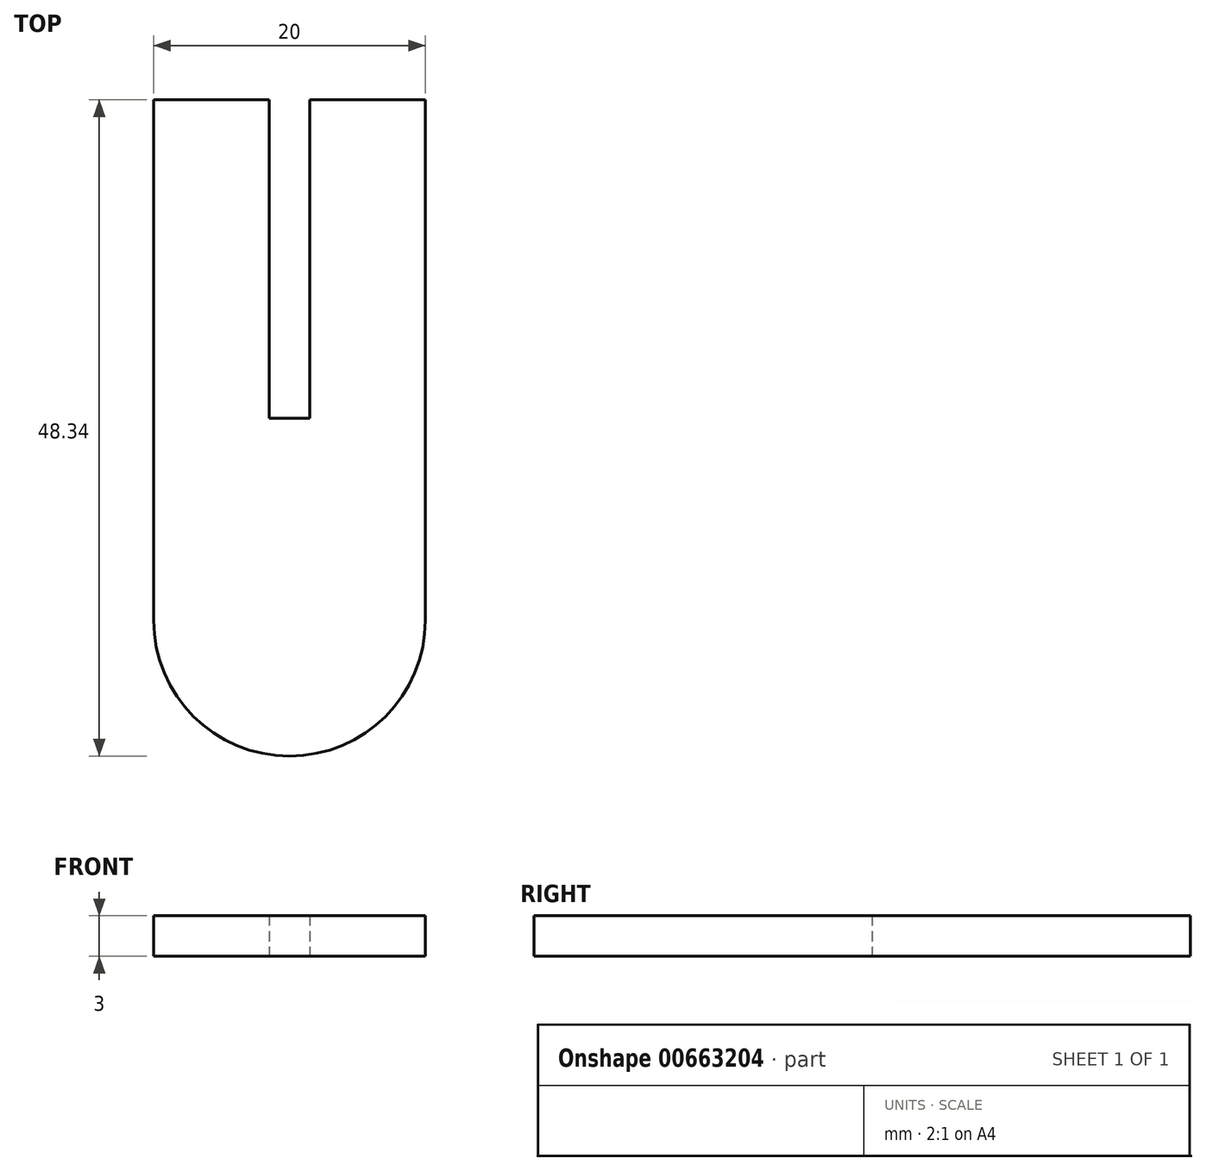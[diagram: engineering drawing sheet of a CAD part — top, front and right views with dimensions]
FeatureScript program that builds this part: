
annotation { "Feature Type Name" : "Feature", "Feature Type Description" : "" }
export const myFeature = defineFeature(function(context is Context, id is Id, definition is map)
    precondition{}
    {
        {
            var Q0;
            Q0=qCreatedBy(makeId("Top.planeOp"),FACE);
            var sketch = newSketch(context, id + "F0", { "sketchPlane" : qUnion([Q0])});
            skLineSegment(sketch, "E0.bottom", {"start": v(-10, 19.17) * mm, "end": v(10, 19.17) * mm});
            skLineSegment(sketch, "E0.top", {"start": v(-10, -19.17) * mm, "end": v(10, -19.17) * mm});
            skLineSegment(sketch, "E0.left", {"start": v(-10, 19.17) * mm, "end": v(-10, -19.17) * mm});
            skLineSegment(sketch, "E0.right", {"start": v(10, 19.17) * mm, "end": v(10, -19.17) * mm});
            skPoint(sketch, "E0.middle", {"position": v(0, 0) * mm});
            skLineSegment(sketch, "E1.bottom", {"start": v(-1.5, 19.17) * mm, "end": v(1.5, 19.17) * mm});
            skLineSegment(sketch, "E1.top", {"start": v(-1.5, -4.28) * mm, "end": v(1.5, -4.28) * mm});
            skLineSegment(sketch, "E1.left", {"start": v(-1.5, 19.17) * mm, "end": v(-1.5, -4.28) * mm});
            skLineSegment(sketch, "E1.right", {"start": v(1.5, 19.17) * mm, "end": v(1.5, -4.28) * mm});
            skPoint(sketch, "E1.middle", {"position": v(0, 7.44) * mm});
            skArc(sketch, "E2", {"start": v(-10, -19.17) * mm, "mid": v(0, -29.17) * mm, "end": v(10, -19.17) * mm});
            skSolve(sketch);
        }
        {
            var Q0;
            Q0=makeQuery(id+"F0.imprint","IMPRINT",FACE,{"disambiguationData":[TD([[makeQuery(id+"F0.imprint","IMPRINT",EDGE,{"derivedFrom":sQuery(id+"F0.wireOp",EDGE,"E0.top")}),1.0]])]});
            var Q1;
            Q1=makeQuery(id+"F0.imprint","IMPRINT",FACE,{"disambiguationData":[TD([[makeQuery(id+"F0.imprint","IMPRINT",EDGE,{"derivedFrom":sQuery(id+"F0.wireOp",EDGE,"E0.top")}),-1.0]])]});
            extrude(context, id + "F1", {"entities" : qUnion([Q0, Q1]), "depth" : 3 * mm, "offsetDistance" : 25 * mm});
        }
    });
